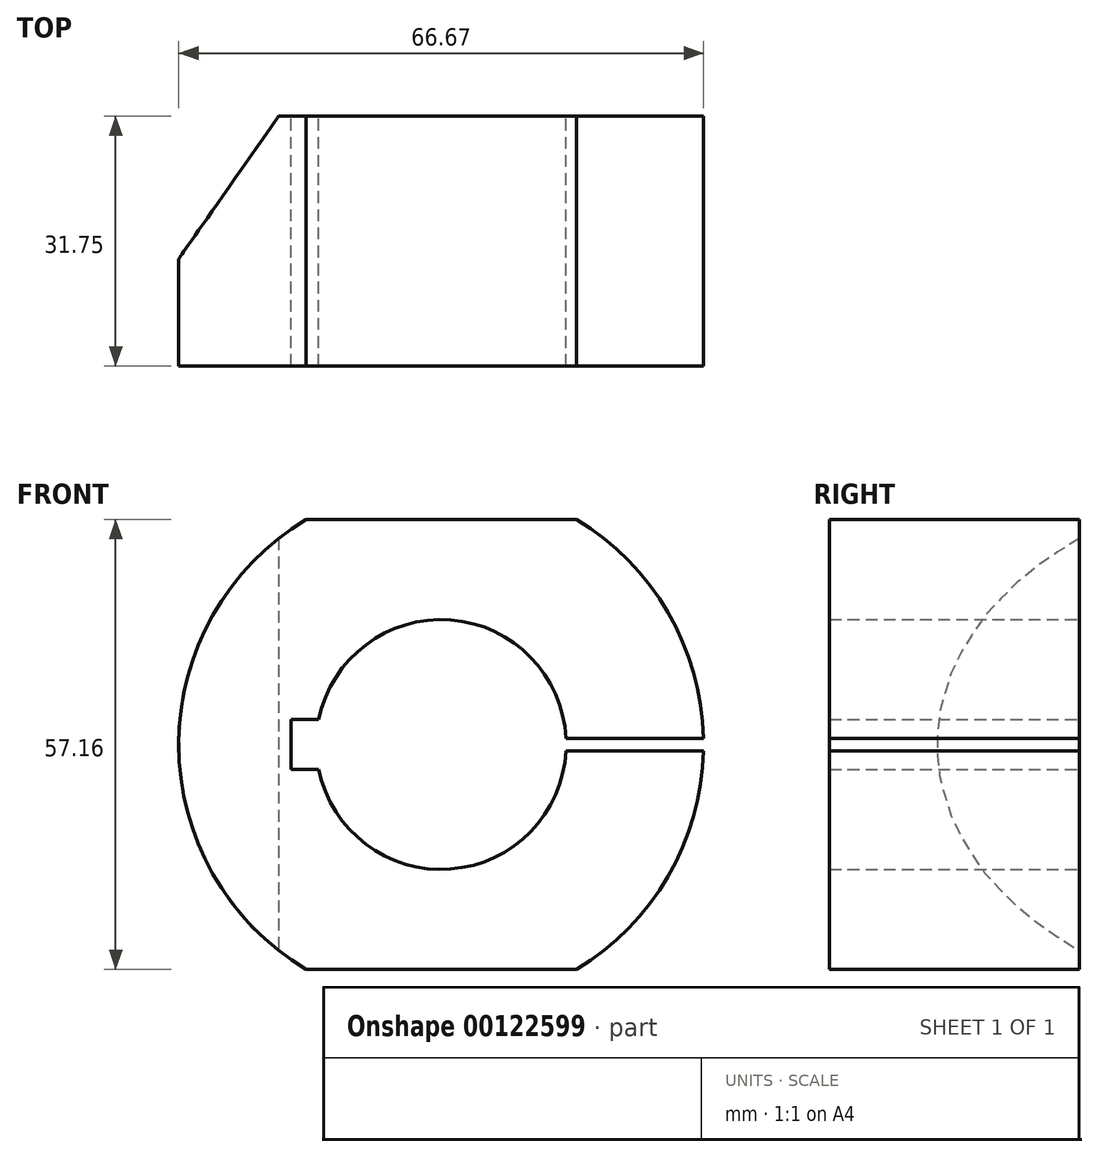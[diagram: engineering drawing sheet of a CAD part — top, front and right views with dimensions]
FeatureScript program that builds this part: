
annotation { "Feature Type Name" : "Feature", "Feature Type Description" : "" }
export const myFeature = defineFeature(function(context is Context, id is Id, definition is map)
    precondition{}
    {
        {
            var Q0;
            Q0=qCreatedBy(makeId("Front.planeOp"),FACE);
            var sketch = newSketch(context, id + "F0", { "sketchPlane" : qUnion([Q0])});
            skArc(sketch, "E0", {"start": v(33.33, 0.8) * mm, "mid": v(28.82, 16.76) * mm, "end": v(17.17, 28.57) * mm});
            skArc(sketch, "E1", {"start": v(15.86, 0.8) * mm, "mid": v(1.2, 15.83) * mm, "end": v(-15.55, 3.17) * mm});
            skLineSegment(sketch, "E2.right", {"start": v(-19.05, -3.18) * mm, "end": v(-19.05, 3.17) * mm});
            skLineSegment(sketch, "E3.trimOffspring", {"start": v(-15.55, 3.17) * mm, "end": v(-19.05, 3.18) * mm});
            skLineSegment(sketch, "E4.trimOffspring", {"start": v(-15.55, -3.18) * mm, "end": v(-19.05, -3.18) * mm});
            skLineSegment(sketch, "E5.trimOffspring", {"start": v(15.86, 0.8) * mm, "end": v(33.33, 0.8) * mm});
            skLineSegment(sketch, "E6.trimOffspring", {"start": v(15.86, -0.8) * mm, "end": v(33.33, -0.8) * mm});
            skArc(sketch, "E7.trimOffspring", {"start": v(-15.55, -3.17) * mm, "mid": v(1.2, -15.83) * mm, "end": v(15.86, -0.8) * mm});
            skLineSegment(sketch, "E8.0", {"start": v(-17.17, -28.58) * mm, "end": v(17.17, -28.58) * mm});
            skLineSegment(sketch, "E9.0", {"start": v(-17.17, 28.58) * mm, "end": v(17.17, 28.58) * mm});
            skArc(sketch, "E10.trimOffspring", {"start": v(-17.17, 28.57) * mm, "mid": v(-33.34, 0) * mm, "end": v(-17.17, -28.58) * mm});
            skArc(sketch, "E11.trimOffspring", {"start": v(17.17, -28.58) * mm, "mid": v(28.82, -16.76) * mm, "end": v(33.33, -0.8) * mm});
            skSolve(sketch);
        }
        {
            var Q0;
            Q0 = qSketchRegion(id + "F0", true);
            extrude(context, id + "F1", {"entities" : qUnion([Q0]), "depth" : 31.75 * mm});
        }
        {
            var Q0;
            Q0=qCreatedBy(makeId("Top.planeOp"),FACE);
            var sketch = newSketch(context, id + "F2", { "sketchPlane" : qUnion([Q0])});
            skLineSegment(sketch, "E12", {"start": v(0, 6.48) * mm, "end": v(0, -42.37) * mm});
            skLineSegment(sketch, "E13.0", {"start": v(-20.64, 6.48) * mm, "end": v(-20.64, 0) * mm});
            skLineSegment(sketch, "E14", {"start": v(-20.64, 0) * mm, "end": v(-40.8, -28.78) * mm});
            skLineSegment(sketch, "E15", {"start": v(-20.64, 6.48) * mm, "end": v(-46.34, 6.48) * mm});
            skLineSegment(sketch, "E16", {"start": v(-46.34, 6.48) * mm, "end": v(-45.36, -28.78) * mm});
            skLineSegment(sketch, "E17", {"start": v(-45.36, -28.78) * mm, "end": v(-40.8, -28.78) * mm});
            skSolve(sketch);
        }
        {
            var Q0;
            Q0 = qSketchRegion(id + "F2", true);
            extrude(context, id + "F3", {"entities" : qUnion([Q0]), "operationType" : NewBodyOperationType.REMOVE, "endBound" : BoundingType.SYMMETRIC, "depth" : 57.15 * mm});
        }
    });
